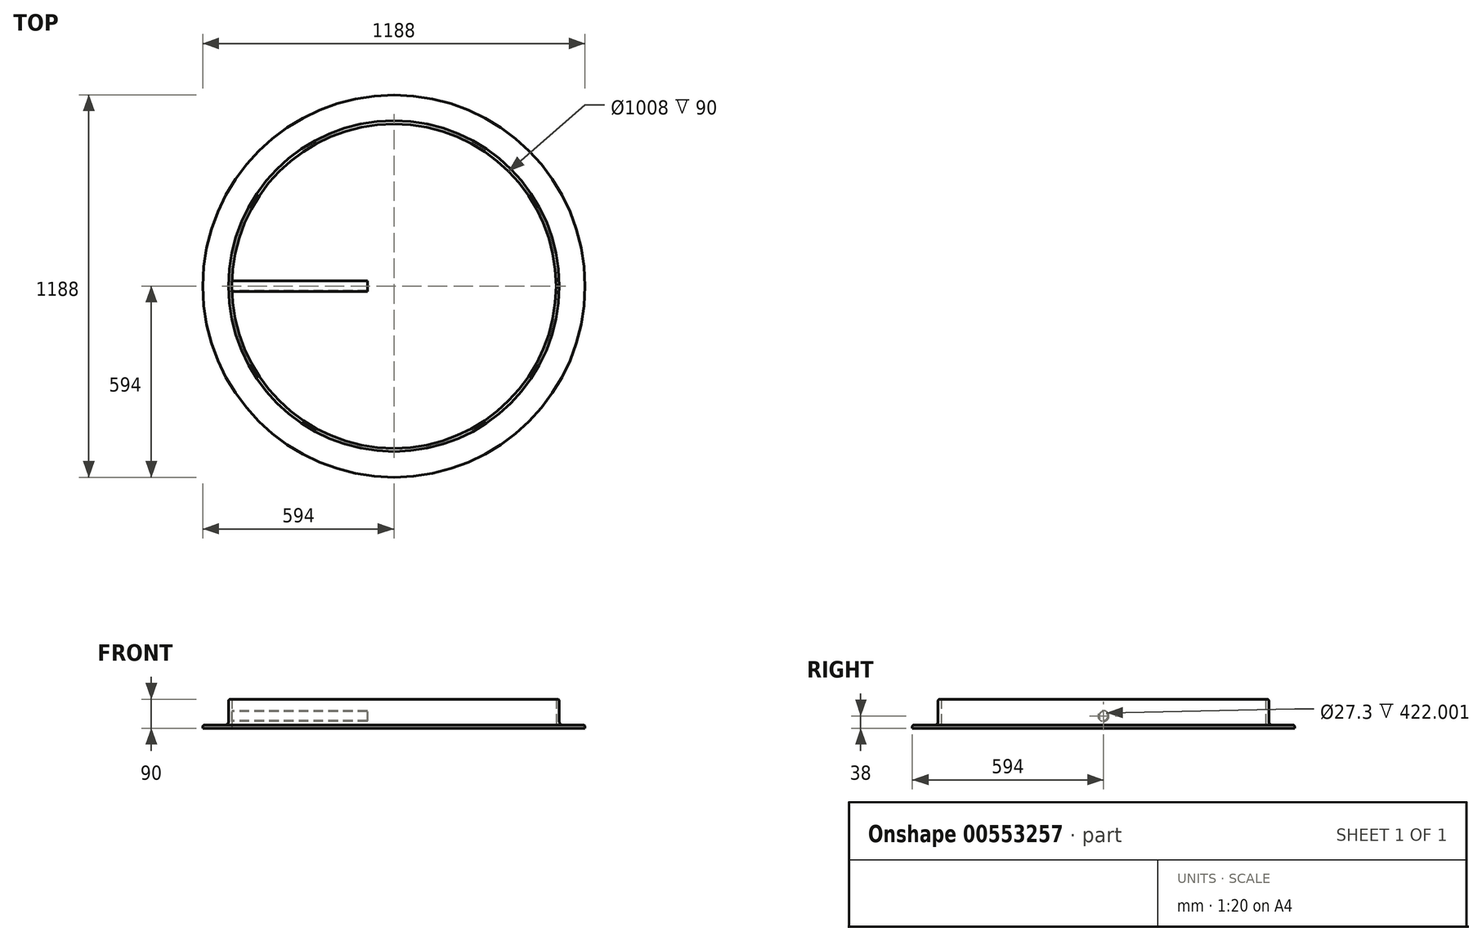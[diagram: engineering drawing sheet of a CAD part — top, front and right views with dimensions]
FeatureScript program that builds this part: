
annotation { "Feature Type Name" : "Feature", "Feature Type Description" : "" }
export const myFeature = defineFeature(function(context is Context, id is Id, definition is map)
    precondition{}
    {
        {
            var Q0;
            Q0=qCreatedBy(makeId("Front.planeOp"),FACE);
            var sketch = newSketch(context, id + "F0", { "sketchPlane" : qUnion([Q0])});
            skLineSegment(sketch, "E0", {"start": v(-90, 0) * mm, "end": v(0, 0) * mm});
            skLineSegment(sketch, "E1", {"start": v(0, 0) * mm, "end": v(0, 90) * mm});
            skLineSegment(sketch, "E2.0", {"start": v(-10, 21) * mm, "end": v(-10, 84.5) * mm});
            skLineSegment(sketch, "E3.0", {"start": v(-84.5, 10) * mm, "end": v(-21, 10) * mm});
            skLineSegment(sketch, "E4", {"start": v(-4.5, 90) * mm, "end": v(0, 90) * mm});
            skLineSegment(sketch, "E5", {"start": v(-90, 4.5) * mm, "end": v(-90, 0) * mm});
            skPoint(sketch, "E6.visualSharp", {"position": v(-10, 90) * mm});
            skArc(sketch, "E6.filletArc", {"start": v(-4.5, 90) * mm, "mid": v(-8.39, 88.39) * mm, "end": v(-10, 84.5) * mm});
            skPoint(sketch, "E7.visualSharp", {"position": v(-90, 10) * mm});
            skArc(sketch, "E7.filletArc", {"start": v(-84.5, 10) * mm, "mid": v(-88.39, 8.39) * mm, "end": v(-90, 4.5) * mm});
            skArc(sketch, "E8.filletArc", {"start": v(-21, 10) * mm, "mid": v(-13.22, 13.22) * mm, "end": v(-10, 21) * mm});
            skLineSegment(sketch, "E9.0", {"start": v(504, 0) * mm, "end": v(504, 90) * mm, "construction": true});
            skSolve(sketch);
        }
        {
            var Q0;
            Q0=makeQuery(id+"F0.imprint","IMPRINT",FACE,{"disambiguationData":[TD([[makeQuery(id+"F0.imprint","IMPRINT",EDGE,{"derivedFrom":sQuery(id+"F0.wireOp",EDGE,"E0")}),1.0]])]});
            var Q1;
            Q1=sQuery(id+"F0.wireOp",EDGE,"E9.0");
            revolve(context, id + "F1", {"entities" : qUnion([Q0]), "axis" : qUnion([Q1]), "revolveType" : RevolveType.FULL});
        }
        {
            var Q0;
            Q0=qCreatedBy(makeId("Right.planeOp"),FACE);
            var sketch = newSketch(context, id + "F2", { "sketchPlane" : qUnion([Q0])});
            skCircle(sketch, "E10", {"center": v(0, 38) * mm, "radius": 16.85 * mm});
            skCircle(sketch, "E11.0", {"center": v(0, 38) * mm, "radius": 13.65 * mm});
            skSolve(sketch);
        }
        {
            var Q0;
            Q0 = qSketchRegion(id + "F2", true);
            extrude(context, id + "F3", {"entities" : qUnion([Q0]), "operationType" : NewBodyOperationType.ADD, "depth" : 422 * mm, "offsetDistance" : 25 * mm});
        }
    });
